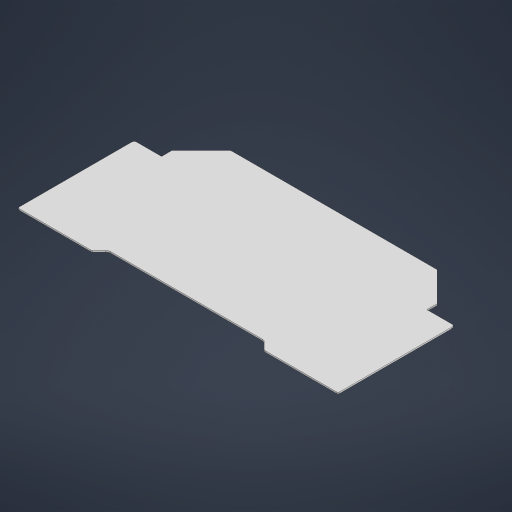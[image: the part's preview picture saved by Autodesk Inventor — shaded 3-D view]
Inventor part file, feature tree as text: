
AUTODESK INVENTOR PART (.ipt)
format: ipt  version: 2024 (Build 280153000, 153)  size: 217,600 bytes
history: native  units: mm
features: other x1, extrude x1, sketch x1
ambient origin geometry x8: Origin, YZ Plane, XZ Plane, XY Plane, X Axis, Y Axis, Z Axis, Center Point
bodies: Body1 (feature_tree)
feature tree (3):
  other  "Těleso1"
  extrude  "Vysunutí1"  Depth=0.5mm
  sketch  "Náčrt1"
